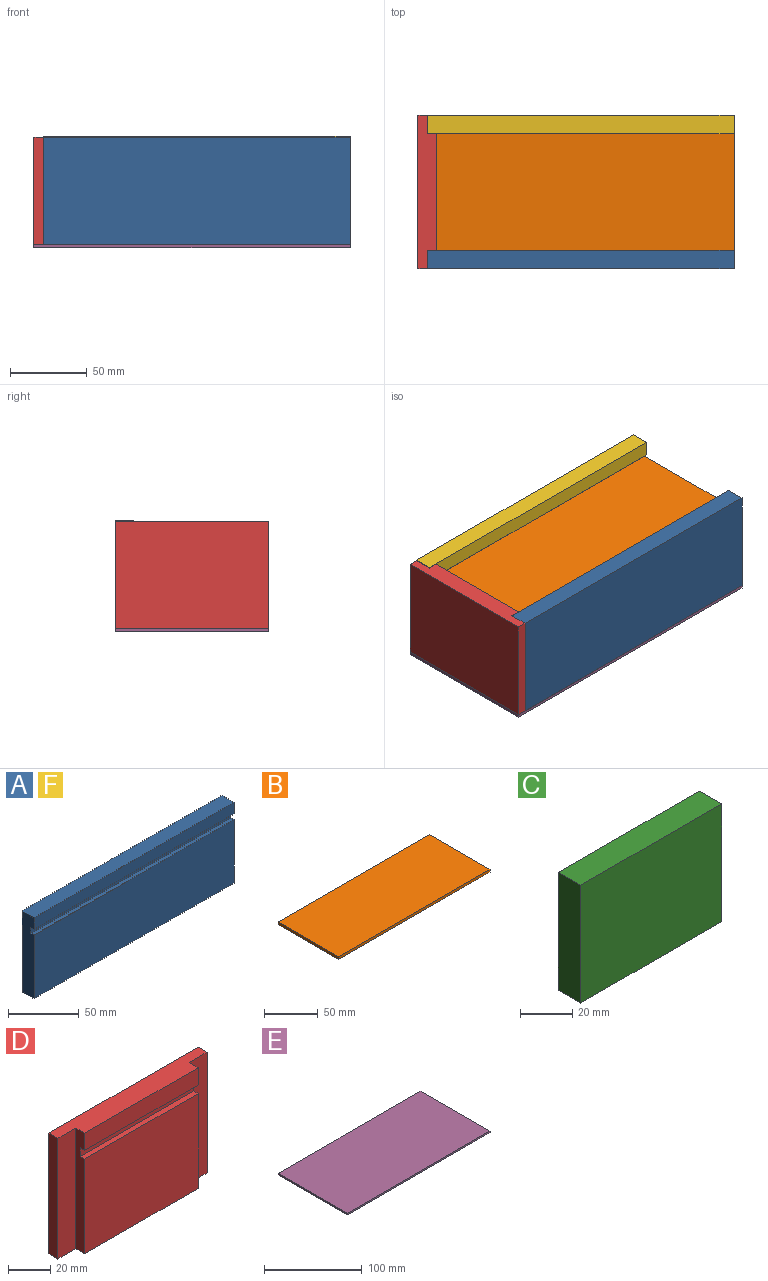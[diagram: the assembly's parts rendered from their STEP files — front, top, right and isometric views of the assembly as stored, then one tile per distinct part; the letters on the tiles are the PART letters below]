
ASSEMBLY  parts=6 mates=5
PART A: 10 faces, bbox 200x12x70 mm
  f0: plane 200x55mm, normal (0,-1,0), area 11000mm2, adj f1,f7,f8,f9
  f1: plane 200x12mm, normal (0,0,-1), area 2400mm2, adj f0,f2,f8,f9
  f2: plane 200x70mm, normal (0,1,0), area 14000mm2, adj f1,f3,f8,f9
  f3: plane 200x12mm, normal (0,0,1), area 2400mm2, adj f2,f4,f8,f9
  f4: plane 200x10mm, normal (0,-1,0), area 2000mm2, adj f3,f5,f8,f9
  f5: plane 200x3mm, normal (0,0,-1), area 600mm2, adj f4,f6,f8,f9
  f6: plane 200x5mm, normal (0,-1,0), area 1000mm2, adj f5,f7,f8,f9
  f7: plane 200x3mm, normal (0,0,1), area 600mm2, adj f0,f6,f8,f9
  f8: plane 70x12mm, normal (1,0,0), area 825mm2, adj f0,f1,f2,f3,f4,f5,f6,f7
  f9: plane 70x12mm, normal (-1,0,0), area 825mm2, adj f0,f1,f2,f3,f4,f5,f6,f7
PART B: 6 faces, bbox 200x80x3 mm
  f0: plane 80x3mm, normal (-1,0,0), area 240mm2, adj f1,f3,f4,f5
  f1: plane 200x3mm, normal (0,-1,0), area 600mm2, adj f0,f2,f4,f5
  f2: plane 80x3mm, normal (1,0,0), area 240mm2, adj f1,f3,f4,f5
  f3: plane 200x3mm, normal (0,1,0), area 600mm2, adj f0,f2,f4,f5
  f4: plane 200x80mm, normal (0,0,1), area 16000mm2, adj f0,f1,f2,f3
  f5: plane 200x80mm, normal (0,0,-1), area 16000mm2, adj f0,f1,f2,f3
PART C: 6 faces, bbox 76x12x55 mm
  f0: plane 55x12mm, normal (-1,0,0), area 660mm2, adj f1,f3,f4,f5
  f1: plane 76x12mm, normal (0,0,-1), area 912mm2, adj f0,f2,f4,f5
  f2: plane 55x12mm, normal (1,0,0), area 660mm2, adj f1,f3,f4,f5
  f3: plane 76x12mm, normal (0,0,1), area 912mm2, adj f0,f2,f4,f5
  f4: plane 76x55mm, normal (0,-1,0), area 4180mm2, adj f0,f1,f2,f3
  f5: plane 76x55mm, normal (0,1,0), area 4180mm2, adj f0,f1,f2,f3
PART D: 14 faces, bbox 100x12x70 mm
  f0: plane 100x12mm, normal (0,0,1), area 1056mm2, adj f1,f7,f8,f9,f10,f11,f12,f13
  f1: plane 76x10mm, normal (0,-1,0), area 760mm2, adj f0,f3,f10,f12
  f2: plane 76x55mm, normal (0,-1,0), area 4180mm2, adj f5,f6,f10,f12
  f3: plane 76x3mm, normal (0,0,-1), area 228mm2, adj f1,f4,f10,f12
  f4: plane 76x5mm, normal (0,-1,0), area 380mm2, adj f3,f5,f10,f12
  f5: plane 76x3mm, normal (0,0,1), area 228mm2, adj f2,f4,f10,f12
  f6: plane 100x12mm, normal (0,0,-1), area 1056mm2, adj f2,f7,f8,f9,f10,f11,f12,f13
  f7: plane 100x70mm, normal (0,1,0), area 7000mm2, adj f0,f6,f8,f9
  f8: plane 70x6mm, normal (1,0,0), area 420mm2, adj f0,f6,f7,f13
  f9: plane 70x6mm, normal (-1,0,0), area 420mm2, adj f0,f6,f7,f11
  f10: plane 70x6mm, normal (-1,0,0), area 405mm2, adj f0,f1,f2,f3,f4,f5,f6,f11
  f11: plane 70x12mm, normal (0,-1,0), area 840mm2, adj f0,f6,f9,f10
  f12: plane 70x6mm, normal (1,0,0), area 405mm2, adj f0,f1,f2,f3,f4,f5,f6,f13
  f13: plane 70x12mm, normal (0,-1,0), area 840mm2, adj f0,f6,f8,f12
PART E: 6 faces, bbox 206x100x2 mm
  f0: plane 100x2mm, normal (-1,0,0), area 200mm2, adj f1,f3,f4,f5
  f1: plane 206x2mm, normal (0,-1,0), area 412mm2, adj f0,f2,f4,f5
  f2: plane 100x2mm, normal (1,0,0), area 200mm2, adj f1,f3,f4,f5
  f3: plane 206x2mm, normal (0,1,0), area 412mm2, adj f0,f2,f4,f5
  f4: plane 206x100mm, normal (0,0,1), area 20600mm2, adj f0,f1,f2,f3
  f5: plane 206x100mm, normal (0,0,-1), area 20600mm2, adj f0,f1,f2,f3
PART F: same geometry as A
PLACE A rot(axis=(0,0,1),180deg) t=(49.44,-157.84,-16.7)mm
PLACE B rot(axis=(1,0,0),180deg) t=(-150.56,-79.92,41.71)mm
PLACE C rot(axis=(0,0,1),90deg) t=(37.44,-157.92,-16.29)mm
PLACE D rot(axis=(0,0,1),90deg) t=(-156.56,-169.84,-16.7)mm
PLACE E t=(-156.56,-169.84,-18.7)mm
PLACE F t=(-150.56,-81.92,-16.29)mm
MATE fastened B.f4 <-> C.f3  axis (0,0,-1) through (49.44,-119.92,38.71)mm
MATE fastened C.f2 <-> F.f0  axis (0,1,0) through (49.44,-81.92,11.21)mm
MATE fastened E.f4 <-> D.f6  axis (0,0,1) through (-156.56,-169.84,-16.7)mm
MATE fastened D.f13 <-> F.f9  axis (1,0,0) through (-150.56,-75.84,18.3)mm
MATE fastened A.f8 <-> D.f11  axis (-1,0,0) through (-150.56,-169.84,53.3)mm
